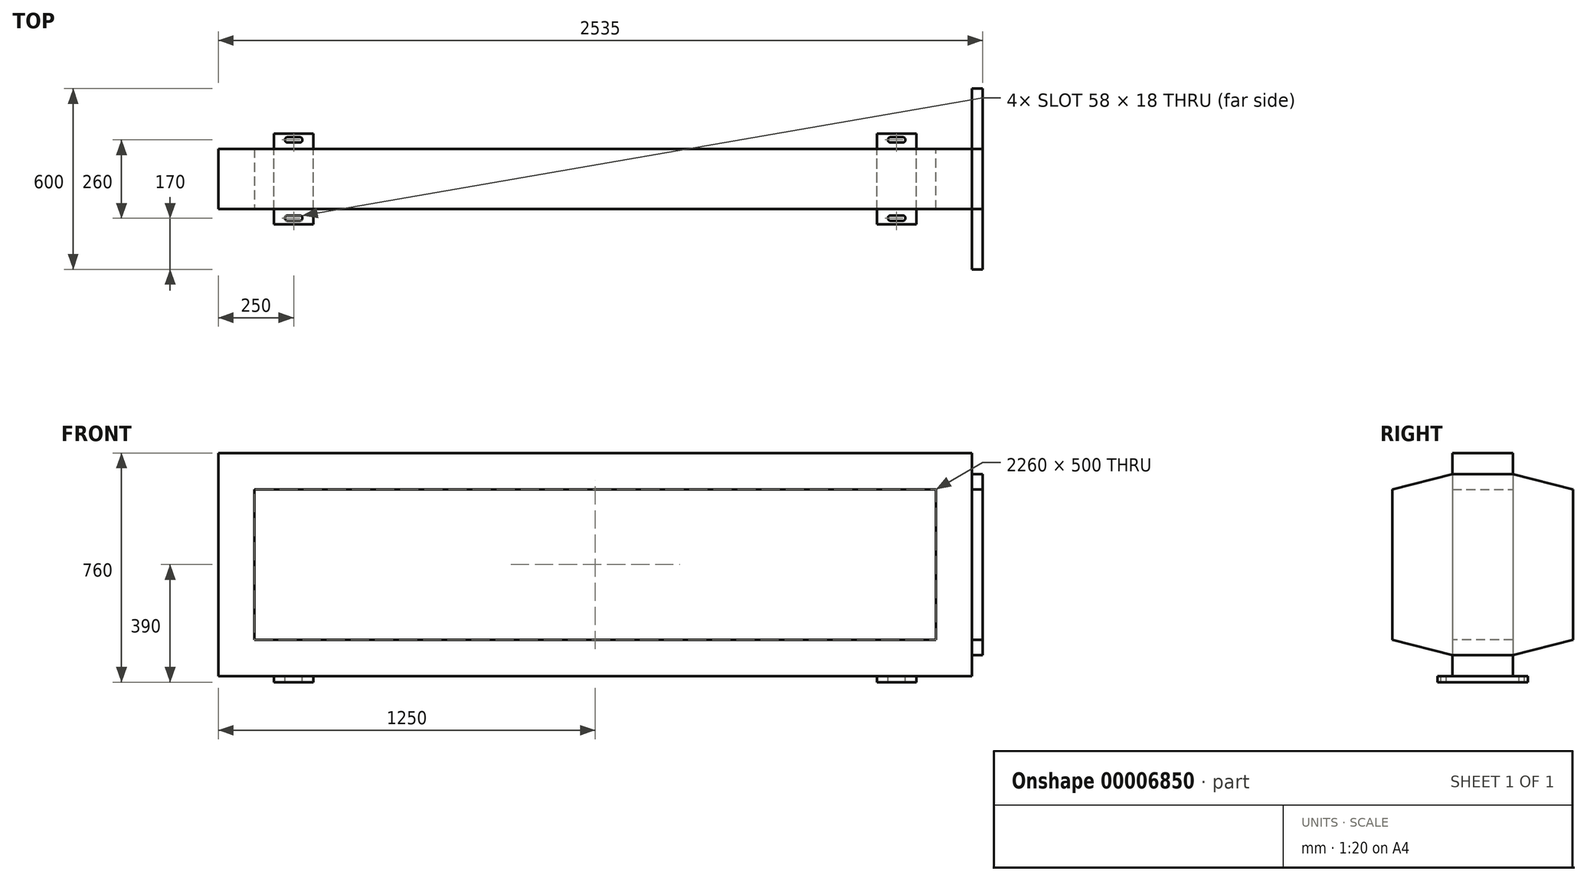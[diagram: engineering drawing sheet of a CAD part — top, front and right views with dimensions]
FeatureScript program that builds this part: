
annotation { "Feature Type Name" : "Feature", "Feature Type Description" : "" }
export const myFeature = defineFeature(function(context is Context, id is Id, definition is map)
    precondition{}
    {
        {
            var Q0;
            Q0=qCreatedBy(makeId("Top.planeOp"),FACE);
            var sketch = newSketch(context, id + "F0", { "sketchPlane" : qUnion([Q0])});
            skLineSegment(sketch, "E0.rect.bottom", {"start": v(-1250, 100) * mm, "end": v(1250, 100) * mm});
            skLineSegment(sketch, "E0.rect.top", {"start": v(-1250, -100) * mm, "end": v(1250, -100) * mm});
            skLineSegment(sketch, "E0.rect.left", {"start": v(-1250, 100) * mm, "end": v(-1250, -100) * mm});
            skLineSegment(sketch, "E0.rect.right", {"start": v(1250, 100) * mm, "end": v(1250, -100) * mm});
            skPoint(sketch, "E0.rect.middle", {"position": v(0, 0) * mm});
            skSolve(sketch);
        }
        {
            var Q0;
            Q0 = qSketchRegion(id + "F0", true);
            extrude(context, id + "F1", {"entities" : qUnion([Q0]), "depth" : 120 * mm});
        }
        {
            var Q0;
            Q0=makeQuery(id+"F1.opExtrude","CAP_FACE",FACE,{"disambiguationData":[OSD([sQuery(id+"F0.wireOp",EDGE,"E0.rect.bottom"),sQuery(id+"F0.wireOp",EDGE,"E0.rect.top"),sQuery(id+"F0.wireOp",EDGE,"E0.rect.left"),sQuery(id+"F0.wireOp",EDGE,"E0.rect.right")])],"isStart":true});
            var sketch = newSketch(context, id + "F2", { "sketchPlane" : qUnion([Q0])});
            skLineSegment(sketch, "E1", {"start": v(0, 272.16) * mm, "end": v(0, -313.07) * mm, "construction": true});
            skLineSegment(sketch, "E2.0", {"start": v(-1000, 272.16) * mm, "end": v(-1000, -313.07) * mm, "construction": true});
            skLineSegment(sketch, "E3.0", {"start": v(-1065, 150) * mm, "end": v(-1065, -150) * mm});
            skLineSegment(sketch, "E4", {"start": v(-1395.43, 0) * mm, "end": v(1376.55, 0) * mm, "construction": true});
            skLineSegment(sketch, "E5.0", {"start": v(-1065, -150) * mm, "end": v(-935, -150) * mm});
            skLineSegment(sketch, "E6.0.MirrorCS", {"start": v(-1065, 150) * mm, "end": v(-935, 150) * mm});
            skLineSegment(sketch, "E7.0.MirrorCS", {"start": v(-935, 150) * mm, "end": v(-935, -150) * mm});
            skPoint(sketch, "E8.orphan", {"position": v(-1395.43, 150) * mm});
            skPoint(sketch, "E9.orphan", {"position": v(-1065, 272.16) * mm});
            skPoint(sketch, "E10.orphan", {"position": v(-935, 272.16) * mm});
            skPoint(sketch, "E11.trimOffspring.end.orphan", {"position": v(1376.55, 150) * mm});
            skPoint(sketch, "E12.orphan", {"position": v(1376.55, -150) * mm});
            skPoint(sketch, "E13.orphan", {"position": v(-935, -313.07) * mm});
            skPoint(sketch, "E14.orphan", {"position": v(-1065, -313.07) * mm});
            skPoint(sketch, "E15.orphan", {"position": v(-1395.43, -150) * mm});
            skLineSegment(sketch, "E16.0", {"start": v(-1395.43, -130) * mm, "end": v(1376.55, -130) * mm, "construction": true});
            skLineSegment(sketch, "E17.0", {"start": v(-1020, 272.16) * mm, "end": v(-1020, -313.07) * mm, "construction": true});
            skArc(sketch, "E18", {"start": v(-1020, -121) * mm, "mid": v(-1029, -130) * mm, "end": v(-1020, -139) * mm});
            skArc(sketch, "E19.0.MirrorC", {"start": v(-980, -121) * mm, "mid": v(-971, -130) * mm, "end": v(-980, -139) * mm});
            skLineSegment(sketch, "E20", {"start": v(-1020, -121) * mm, "end": v(-980, -121) * mm});
            skLineSegment(sketch, "E21.0.MirrorCS", {"start": v(-1020, -139) * mm, "end": v(-980, -139) * mm});
            skLineSegment(sketch, "E22.0.MirrorCS", {"start": v(-1020, 121) * mm, "end": v(-980, 121) * mm});
            skArc(sketch, "E23.0.MirrorCS", {"start": v(-980, 121) * mm, "mid": v(-971, 130) * mm, "end": v(-980, 139) * mm});
            skLineSegment(sketch, "E24.0.MirrorCS", {"start": v(-1020, 139) * mm, "end": v(-980, 139) * mm});
            skArc(sketch, "E25.0.MirrorCS", {"start": v(-1020, 121) * mm, "mid": v(-1029, 130) * mm, "end": v(-1020, 139) * mm});
            skLineSegment(sketch, "E26.0.MirrorCS", {"start": v(1020, 121) * mm, "end": v(980, 121) * mm});
            skArc(sketch, "E26.1.MirrorCS", {"start": v(980, 121) * mm, "mid": v(971, 130) * mm, "end": v(980, 139) * mm});
            skLineSegment(sketch, "E26.2.MirrorCS", {"start": v(1020, -121) * mm, "end": v(980, -121) * mm});
            skArc(sketch, "E26.3.MirrorCS", {"start": v(1020, -121) * mm, "mid": v(1029, -130) * mm, "end": v(1020, -139) * mm});
            skArc(sketch, "E26.4.MirrorCS", {"start": v(980, -121) * mm, "mid": v(971, -130) * mm, "end": v(980, -139) * mm});
            skLineSegment(sketch, "E26.5.MirrorCS", {"start": v(1020, 139) * mm, "end": v(980, 139) * mm});
            skArc(sketch, "E26.6.MirrorCS", {"start": v(1020, 121) * mm, "mid": v(1029, 130) * mm, "end": v(1020, 139) * mm});
            skLineSegment(sketch, "E26.7.MirrorCS", {"start": v(1020, -139) * mm, "end": v(980, -139) * mm});
            skLineSegment(sketch, "E26.8.MirrorCS", {"start": v(1065, 150) * mm, "end": v(935, 150) * mm});
            skLineSegment(sketch, "E26.9.MirrorCS", {"start": v(1065, -150) * mm, "end": v(935, -150) * mm});
            skLineSegment(sketch, "E26.10.MirrorCS", {"start": v(935, 150) * mm, "end": v(935, -150) * mm});
            skLineSegment(sketch, "E26.11.MirrorCS", {"start": v(1065, 150) * mm, "end": v(1065, -150) * mm});
            skSolve(sketch);
        }
        {
            var Q0;
            Q0 = qSketchRegion(id + "F2", true);
            extrude(context, id + "F3", {"entities" : qUnion([Q0]), "operationType" : NewBodyOperationType.ADD, "depth" : 20 * mm});
        }
        {
            var Q0;
            Q0=makeQuery(id+"F1.opExtrude","CAP_FACE",FACE,{"disambiguationData":[OSD([sQuery(id+"F0.wireOp",EDGE,"E0.rect.bottom"),sQuery(id+"F0.wireOp",EDGE,"E0.rect.top"),sQuery(id+"F0.wireOp",EDGE,"E0.rect.left"),sQuery(id+"F0.wireOp",EDGE,"E0.rect.right")])],"isStart":false});
            var sketch = newSketch(context, id + "F4", { "sketchPlane" : qUnion([Q0])});
            skLineSegment(sketch, "E27", {"start": v(0, -264) * mm, "end": v(0, 327.28) * mm, "construction": true});
            skLineSegment(sketch, "E28.0.0", {"start": v(1250, 100) * mm, "end": v(1130, 100) * mm});
            skLineSegment(sketch, "E28.0.1", {"start": v(-1250, 100) * mm, "end": v(-1250, -100) * mm});
            skLineSegment(sketch, "E28.0.2", {"start": v(-1250, -100) * mm, "end": v(-1130, -100) * mm});
            skLineSegment(sketch, "E28.0.3", {"start": v(1250, -100) * mm, "end": v(1250, 100) * mm});
            skLineSegment(sketch, "E29.0", {"start": v(1130, -100) * mm, "end": v(1130, 100) * mm});
            skLineSegment(sketch, "E30.0", {"start": v(-1130, 100) * mm, "end": v(-1130, -100) * mm});
            skLineSegment(sketch, "E31.trimOffspring", {"start": v(1130, -100) * mm, "end": v(1250, -100) * mm});
            skLineSegment(sketch, "E32.trimOffspring", {"start": v(-1130, 100) * mm, "end": v(-1250, 100) * mm});
            skSolve(sketch);
        }
        {
            var Q0;
            Q0 = qSketchRegion(id + "F4", true);
            extrude(context, id + "F5", {"entities" : qUnion([Q0]), "operationType" : NewBodyOperationType.ADD, "depth" : 500 * mm});
        }
        {
            var Q0;
            Q0=makeQuery(id+"F5.opExtrude","CAP_FACE",FACE,{"disambiguationData":[OSD([sQuery(id+"F4.wireOp",EDGE,"E28.0.1"),sQuery(id+"F4.wireOp",EDGE,"E28.0.2"),sQuery(id+"F4.wireOp",EDGE,"E30.0"),sQuery(id+"F4.wireOp",EDGE,"E32.trimOffspring")])],"isStart":false});
            var sketch = newSketch(context, id + "F6", { "sketchPlane" : qUnion([Q0])});
            skLineSegment(sketch, "E33.0.1", {"start": v(-1250, -100) * mm, "end": v(1250, -100) * mm});
            skLineSegment(sketch, "E33.0.2", {"start": v(1250, -100) * mm, "end": v(1250, 100) * mm});
            skLineSegment(sketch, "E33.0.3", {"start": v(1250, 100) * mm, "end": v(-1250, 100) * mm});
            skLineSegment(sketch, "E34.0.2", {"start": v(-1250, 100) * mm, "end": v(-1250, -100) * mm});
            skPoint(sketch, "E34.0.3.end.orphan", {"position": v(-1130, -100) * mm});
            skPoint(sketch, "E34.0.1.start.orphan", {"position": v(-1130, 100) * mm});
            skPoint(sketch, "E35.orphan", {"position": v(1130, -100) * mm});
            skPoint(sketch, "E36.orphan", {"position": v(1130, 100) * mm});
            skSolve(sketch);
        }
        {
            var Q0;
            Q0 = qSketchRegion(id + "F6", true);
            extrude(context, id + "F7", {"entities" : qUnion([Q0]), "operationType" : NewBodyOperationType.ADD, "depth" : 120 * mm});
        }
        {
            var Q0;
            Q0=makeQuery(id+"F7.boolean.opBoolean","MERGE",FACE,{"derivedFrom":[makeQuery(id+"F5.boolean.opBoolean","MERGE",FACE,{"derivedFrom":[makeQuery(id+"F1.opExtrude","SWEPT_FACE",FACE,{"disambiguationData":[OSD([sQuery(id+"F0.wireOp",EDGE,"E0.rect.right")])]}),makeQuery(id+"F5.opExtrude","SWEPT_FACE",FACE,{"disambiguationData":[OSD([sQuery(id+"F4.wireOp",EDGE,"E28.0.3")])]})]}),makeQuery(id+"F7.opExtrude","SWEPT_FACE",FACE,{"disambiguationData":[OSD([sQuery(id+"F6.wireOp",EDGE,"E33.0.2")])]})]});
            var sketch = newSketch(context, id + "F8", { "sketchPlane" : qUnion([Q0])});
            skLineSegment(sketch, "E37", {"start": v(-100, 370) * mm, "end": v(244.54, 370) * mm, "construction": true});
            skLineSegment(sketch, "E38", {"start": v(0, 740) * mm, "end": v(0, -124.52) * mm, "construction": true});
            skLineSegment(sketch, "E39.0", {"start": v(-300, 620) * mm, "end": v(-300, 120) * mm});
            skLineSegment(sketch, "E40.0", {"start": v(-100, 740) * mm, "end": v(-100, -124.52) * mm});
            skLineSegment(sketch, "E41.0", {"start": v(-100, 670) * mm, "end": v(0, 670) * mm});
            skLineSegment(sketch, "E42.0", {"start": v(-300, 620) * mm, "end": v(244.54, 620) * mm, "construction": true});
            skLineSegment(sketch, "E43", {"start": v(-300, 620) * mm, "end": v(-100, 670) * mm});
            skLineSegment(sketch, "E44.0.MirrorCS", {"start": v(-100, 70) * mm, "end": v(0, 70) * mm});
            skLineSegment(sketch, "E45.0.MirrorCS", {"start": v(-300, 120) * mm, "end": v(-100, 70) * mm});
            skLineSegment(sketch, "E46.0.MirrorCS", {"start": v(100, 670) * mm, "end": v(0, 670) * mm});
            skLineSegment(sketch, "E47.0.MirrorCS", {"start": v(300, 620) * mm, "end": v(100, 670) * mm});
            skLineSegment(sketch, "E48.0.MirrorCS", {"start": v(300, 620) * mm, "end": v(300, 120) * mm});
            skLineSegment(sketch, "E49.0.MirrorCS", {"start": v(300, 120) * mm, "end": v(100, 70) * mm});
            skLineSegment(sketch, "E50.0.MirrorCS", {"start": v(100, 70) * mm, "end": v(0, 70) * mm});
            skSolve(sketch);
        }
        {
            var Q0;
            Q0 = qSketchRegion(id + "F8", true);
            extrude(context, id + "F9", {"entities" : qUnion([Q0]), "operationType" : NewBodyOperationType.ADD, "depth" : 35 * mm});
        }
    });
